# Revit family: WashBasin-CounterTop-RoundBowl-38cm-WithoutTapHole-Vitra-GeoSeries-7421
name_source: partatom
category: Plumbing Fixtures
revit_build: Autodesk Revit 2017 (Build: 20160225_1515(x64)
units: mm (PartAtom-declared; Revit-internal decimal feet)

## family parameters
Cut with Voids When Loaded = No
Host = Face
OmniClass Number = 23.45.05.14.14
OmniClass Title = Sinks/Lavatories
Part Type = Normal
Room Calculation Point = No
Round Connector Dimension = Use Diameter
Shared = Yes

## types (3) — shared parameters
BIMobject category = Sanitary - Basins
Brand = VitrA
CW Connection = No
Color = White
Default Elevation = 800 mm
Description = VitrA Geo, Round Bowl, Countertop Bowl
Design country = Turkey
HW Connection = No
IFC Classification = Sanitary Terminal
Main Material = Ceramic
Manufacturer = Vitra
Manufacturer name = Vitra
Masterformat 2014 Code = 22 41 16
Masterformat 2014 Description = Residential Lavatories and Sinks
Mounting type = Counter Top Washbasins
NBS Referans Code = 35-65-70-94
NBS Referans Description = Wash Basin Systems
Nominal Depth (mm) = 380 mm
Nominal Height (mm) = 150 mm
Nominal Width (mm) = 380 mm
OmniClass Code = 23.45.05.14.14
OmniClass Description = Sinks/Lavatories
Primary Material = White
Product certification = https://www.vitraglobal.com
Product family = Counter Top Washbasins
Product group = Geo
Secondary Material = White
URL = https://vitraglobal.com
Uniclass 1.4 Code = L7212
Uniclass 1.4 Description = Washbasins
Uniclass 2.0 Code = SS-35-65-70-94
Uniclass 2.0 Description = Sanitary Dispensing And Disposal Units
Uniclass 2015 Code = Pr_40_20_96_81
Uniclass 2015 Name = Wash basins, Sinks and troughs
Uniformat II Code = D2010
Uniformat II Description = Plumbing Fixtures
Vent Connection = No
Warranty Period (Year) = 10 Years
Waste Connection = Yes
Weight Net (kg) = 8.45
Youtube = https://www.youtube.com

## per-type parameters (varying)
| type | Article No. (default) | Model | Product SKU | Product url | Technical description |
| WashBasin-RoundBowl-38cm-CounterTop-Vitra-GeoSeries_7421B003H0016 | 7421B003H0016 | 7421B003H0016 | 7421B003H0016 | https://www.vitra-india.com | https://www.vitra-india.com |
| WashBasin-RoundBowl-38cm-CounterTop-Vitra-GeoSeries_7421B403-0016 | 7421B403-0016 | 7421B403-0016 | 7421B403-0016 | https://www.vitra.co.uk | https://www.vitra.co.uk |
| WashBasin-RoundBowl-38cm-CounterTop-Vitra-GeoSeries_7421B003-0016 | 7421B003-0016 | 7421B003-0016 | 7421B003-0016 | https://www.vitra.co.uk | https://www.vitra.co.uk |

## geometry (parser evidence)
native form markers: Sweep x2
no freeform markers — native parametric forms only
